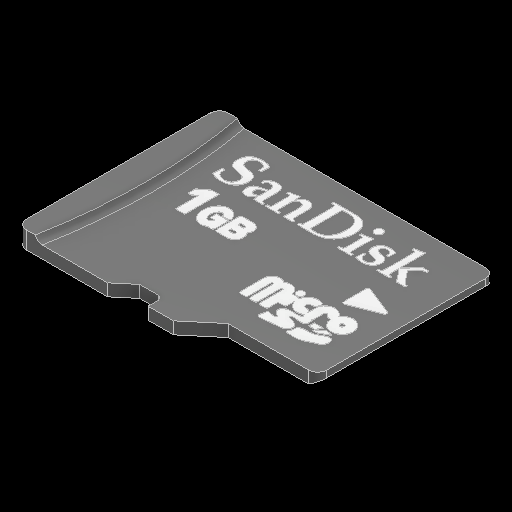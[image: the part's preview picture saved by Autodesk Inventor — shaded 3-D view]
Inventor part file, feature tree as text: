
AUTODESK INVENTOR PART (.ipt)
format: ipt  version: 2022 (Build 260153000, 153)  size: 705,536 bytes
history: native  units: in
note: dims shown in document units (in); Inventor stores cm internally (conversion verified against a paired STEP export)
features: chamfer x1
ambient origin geometry x8: Origin, YZ Plane, XZ Plane, XY Plane, X Axis, Y Axis, Z Axis, Center Point
bodies: Solid1 (feature_tree)
feature tree (1):
  chamfer  "Chamfer1"  [1 undecoded]
note: 1 required parameter value undecoded (feature->parameter linkage not recoverable at this tier; creation-order binding heuristic only, values carry confidence <= 0.55)
